FCSTD DOCUMENT  (FreeCAD 0.17R13541 (Git))
Label: Infineon_PG-LLGA-5-1
License: All rights reserved
LicenseURL: http://en.wikipedia.org/wiki/All_rights_reserved
objects: Sketcher::SketchObject×16, App::Annotation×2, App::DocumentObjectGroup×1
note: 16 computed .brp shape members not serialized (recipe doc carries the construction recipe); baked Part::Feature solids carry a one-line shape summary decoded from their .brp

FEATURE [Sketcher::SketchObject] Sketch  label="F_Fab_0.1"
  sketch-geometry (5):
    g0: LineSegment StartX=2 StartY=1.5 StartZ=0 EndX=2 EndY=-1.5 EndZ=0
    g1: LineSegment StartX=2 StartY=-1.5 StartZ=0 EndX=-2 EndY=-1.5 EndZ=0
    g2: LineSegment StartX=-2 StartY=-1.5 StartZ=0 EndX=-2 EndY=0.5 EndZ=0
    g3: LineSegment StartX=2 StartY=1.5 StartZ=0 EndX=-1 EndY=1.5 EndZ=0
    g4: LineSegment StartX=-2 StartY=0.5 StartZ=0 EndX=-1 EndY=1.5 EndZ=0
  constraints (14):
    c: Coincident(g0,g1)
    c: Coincident(g1,g2)
    c: Horizontal(g1)
    c: Vertical(g0)
    c: Vertical(g2)
    c: Symmetric(g1,g0,g-1)
    c: DistanceY(g0,g0) = 3
    c: DistanceX(g1,g0) = 4
    c: DistanceY(g2,g0) = 1
    c: Coincident(g3,g0)
    c: Horizontal(g3)
    c: DistanceX(g2,g3) = 1
    c: Coincident(g4,g2)
    c: Coincident(g4,g3)
FEATURE [Sketcher::SketchObject] Sketch001  label="F_CrtYd_0.05"
  MapMode = 2
  Support = -> [Sketch]
  sketch-geometry (4):
    g0: LineSegment StartX=-2.25 StartY=1.75 StartZ=0 EndX=2.25 EndY=1.75 EndZ=0
    g1: LineSegment StartX=2.25 StartY=1.75 StartZ=0 EndX=2.25 EndY=-1.75 EndZ=0
    g2: LineSegment StartX=2.25 StartY=-1.75 StartZ=0 EndX=-2.25 EndY=-1.75 EndZ=0
    g3: LineSegment StartX=-2.25 StartY=-1.75 StartZ=0 EndX=-2.25 EndY=1.75 EndZ=0
  constraints (11):
    c: Coincident(g0,g1)
    c: Coincident(g1,g2)
    c: Coincident(g2,g3)
    c: Coincident(g3,g0)
    c: Horizontal(g0)
    c: Horizontal(g2)
    c: Vertical(g1)
    c: Vertical(g3)
    c: DistanceX(g2,g2) = 4.5
    c: DistanceY(g1,g1) = 3.5
    c: Symmetric(g1,g0,g-1)
FEATURE [Sketcher::SketchObject] Sketch002  label="F_Silks_0.12"
  MapMode = 2
  Support = -> [Sketch001]
  sketch-geometry (4):
    g0: LineSegment StartX=-2.11 StartY=1.61 StartZ=0 EndX=2.11 EndY=1.61 EndZ=0
    g1: LineSegment StartX=2.11 StartY=1.61 StartZ=0 EndX=2.11 EndY=-1.61 EndZ=0
    g2: LineSegment StartX=2.11 StartY=-1.61 StartZ=0 EndX=-2.11 EndY=-1.61 EndZ=0
    g3: LineSegment StartX=-2.11 StartY=-1.61 StartZ=0 EndX=-2.11 EndY=1.61 EndZ=0
  constraints (11):
    c: Coincident(g0,g1)
    c: Coincident(g1,g2)
    c: Coincident(g2,g3)
    c: Coincident(g3,g0)
    c: Horizontal(g0)
    c: Horizontal(g2)
    c: Vertical(g1)
    c: Vertical(g3)
    c: DistanceX(g2,g2) = 4.22
    c: DistanceY(g1,g1) = 3.22
    c: Symmetric(g1,g0,g-1)
FEATURE [Sketcher::SketchObject] Sketch003  label="Pads_NPTH"
  sketch-geometry (1):
    g0: Circle CenterX=0.68 CenterY=0 CenterZ=0 NormalX=0 NormalY=0 NormalZ=1 AngleXU=0 Radius=0.4
  constraints (3):
    c: PointOnObject(g0,g-1)
    c: Radius(g0) = 0.4
    c: DistanceX(g-1,g0) = 0.68
FEATURE [Sketcher::SketchObject] Sketch005  label="Pads_TH_SMD"
  MapMode = 2
  sketch-geometry (19):
    g0: LineSegment StartX=-1.275 StartY=1.2 StartZ=0 EndX=-1.725 EndY=1.2 EndZ=0
    g1: LineSegment StartX=-1.725 StartY=1.2 StartZ=0 EndX=-1.725 EndY=0.5 EndZ=0
    g2: LineSegment StartX=-1.725 StartY=0.5 StartZ=0 EndX=-1.275 EndY=0.5 EndZ=0
    g3: LineSegment StartX=-1.275 StartY=0.5 StartZ=0 EndX=-1.275 EndY=1.2 EndZ=0
    g4: GeomPoint X=-1.5 Y=0.5 Z=0
    g5: GeomPoint X=-1.725 Y=0.85 Z=0
    g6: LineSegment StartX=-1.025 StartY=1.2 StartZ=0 EndX=-0.575 EndY=1.2 EndZ=0
    g7: LineSegment StartX=-0.575 StartY=1.2 StartZ=0 EndX=-0.575 EndY=0.5 EndZ=0
    g8: LineSegment StartX=-0.575 StartY=0.5 StartZ=0 EndX=-1.025 EndY=0.5 EndZ=0
    g9: LineSegment StartX=-1.025 StartY=0.5 StartZ=0 EndX=-1.025 EndY=1.2 EndZ=0
    g10: LineSegment StartX=-1.725 StartY=-0.5 StartZ=0 EndX=-1.275 EndY=-0.5 EndZ=0
    g11: LineSegment StartX=-1.275 StartY=-0.5 StartZ=0 EndX=-1.275 EndY=-1.2 EndZ=0
    g12: LineSegment StartX=-1.275 StartY=-1.2 StartZ=0 EndX=-1.725 EndY=-1.2 EndZ=0
    g13: LineSegment StartX=-1.725 StartY=-1.2 StartZ=0 EndX=-1.725 EndY=-0.5 EndZ=0
    g14: LineSegment StartX=-1.025 StartY=-0.5 StartZ=0 EndX=-0.575 EndY=-0.5 EndZ=0
    g15: LineSegment StartX=-0.575 StartY=-0.5 StartZ=0 EndX=-0.575 EndY=-1.2 EndZ=0
    g16: LineSegment StartX=-0.575 StartY=-1.2 StartZ=0 EndX=-1.025 EndY=-1.2 EndZ=0
    g17: LineSegment StartX=-1.025 StartY=-1.2 StartZ=0 EndX=-1.025 EndY=-0.5 EndZ=0
    g18: GeomPoint X=-1.725 Y=-0.85 Z=0
  constraints (54):
    c: Coincident(g0,g1)
    c: Coincident(g1,g2)
    c: Coincident(g2,g3)
    c: Coincident(g3,g0)
    c: Horizontal(g0)
    c: Horizontal(g2)
    c: Vertical(g1)
    c: Vertical(g3)
    c: DistanceX(g2,g2) = 0.45
    c: DistanceY(g3,g3) = 0.7
    c: PointOnObject(g4,g2)
    c: Symmetric(g2,g1,g4)
    c: PointOnObject(g5,g1)
    c: Symmetric(g0,g1,g5)
    c: DistanceY(g-1,g5) = 0.85
    c: DistanceX(g4,g-1) = 1.5
    c: Coincident(g6,g7)
    c: Coincident(g7,g8)
    c: Coincident(g8,g9)
    c: Coincident(g9,g6)
    c: Horizontal(g6)
    c: Horizontal(g8)
    c: Vertical(g7)
    c: Vertical(g9)
    c: Coincident(g10,g11)
    c: Coincident(g11,g12)
    c: Coincident(g12,g13)
    c: Coincident(g13,g10)
    c: Horizontal(g10)
    c: Horizontal(g12)
    c: Vertical(g11)
    c: Vertical(g13)
    c: Coincident(g14,g15)
    c: Coincident(g15,g16)
    c: Coincident(g16,g17)
    c: Coincident(g17,g14)
    c: Horizontal(g14)
    c: Horizontal(g16)
    c: Vertical(g15)
    c: Vertical(g17)
    c: Equal(g3,g7)
    c: Equal(g7,g15)
    c: Equal(g15,g11)
    c: Equal(g2,g8)
    c: Equal(g8,g14)
    c: Equal(g14,g10)
    c: PointOnObject(g18,g13)
    c: Symmetric(g12,g10,g18)
    c: DistanceY(g18,g5) = 1.7
    c: DistanceY(g0,g6) = 0
    c: DistanceX(g10,g2) = 0
    c: DistanceX(g14,g8) = 0
    c: DistanceY(g10,g14) = 0
    c: DistanceX(g2,g7) = 0.7
FEATURE [Sketcher::SketchObject] Sketch006  label="Pads_Poly_paste"
  MapMode = 2
  Support = -> [Sketch005]
  sketch-geometry (8):
    g0: ArcOfCircle CenterX=-1.5 CenterY=0.975 CenterZ=0 NormalX=0 NormalY=0 NormalZ=1 AngleXU=0 Radius=0.2 StartAngle=0 EndAngle=3.14159
    g1: ArcOfCircle CenterX=-1.5 CenterY=0.725 CenterZ=0 NormalX=0 NormalY=0 NormalZ=1 AngleXU=0 Radius=0.2 StartAngle=3.14159 EndAngle=6.28319
    g2: LineSegment StartX=-1.7 StartY=0.975 StartZ=0 EndX=-1.7 EndY=0.725 EndZ=0
    g3: LineSegment StartX=-1.3 StartY=0.975 StartZ=0 EndX=-1.3 EndY=0.725 EndZ=0
    g4: GeomPoint X=-1.5 Y=1.175 Z=0
    g5: GeomPoint X=-1.5 Y=0.525 Z=0
    g6: GeomPoint X=-1.5 Y=0.85 Z=0
    g7: Circle CenterX=-1.5 CenterY=0.725 CenterZ=0 NormalX=0 NormalY=0 NormalZ=1 AngleXU=0 Radius=0.15
  constraints (17):
    c: Tangent(g0,g3) = 1.5708
    c: Tangent(g0,g2) = -1.5708
    c: Tangent(g2,g1) = -1.5708
    c: Tangent(g3,g1) = 1.5708
    c: Vertical(g2)
    c: Equal(g0,g1)
    c: DistanceX(g0,g0) = 0.4
    c: PointOnObject(g4,g0)
    c: PointOnObject(g5,g1)
    c: Vertical(g5,g1)
    c: Vertical(g0,g4)
    c: DistanceY(g5,g4) = 0.65
    c: DistanceX(g5,g-1) = 1.5
    c: Symmetric(g0,g1,g6)
    c: DistanceY(g-1,g6) = 0.85
    c: Coincident(g7,g1)
    c: Radius(g7) = 0.15
FEATURE [App::Annotation] Text  label="Ref#_1mm"
  LabelText = REF**
  Position = (0,2.5,0)
FEATURE [App::Annotation] Text001  label="Value#_1.00mm"
  LabelText = Infineon_PG-LLGA-5-1
  Position = (0,-2.5,0)
FEATURE [Sketcher::SketchObject] Sketch008  label="Pads_Geom_0.46"
  MapMode = 2
  sketch-geometry (2):
    g0: Circle CenterX=0.68 CenterY=0 CenterZ=0 NormalX=0 NormalY=0 NormalZ=1 AngleXU=0 Radius=0.81
    g1: Circle [constr] CenterX=0.68 CenterY=0.81 CenterZ=0 NormalX=0 NormalY=0 NormalZ=1 AngleXU=0 Radius=0.2
  constraints (6):
    c: Radius(g0) = 0.81
    c: DistanceX(g-1,g0) = 0.68
    c: PointOnObject(g0,g-1)
    c: PointOnObject(g1,g0)
    c: Radius(g1) = 0.2
    c: Vertical(g1,g0)
FEATURE [Sketcher::SketchObject] Sketch009  label="Pads_Poly_paste001"
  MapMode = 2
  Support = -> [Sketch005]
  sketch-geometry (8):
    g0: ArcOfCircle CenterX=-0.8 CenterY=0.975 CenterZ=0 NormalX=0 NormalY=0 NormalZ=1 AngleXU=0 Radius=0.2 StartAngle=0 EndAngle=3.14159
    g1: LineSegment StartX=-1 StartY=0.975 StartZ=0 EndX=-1 EndY=0.725 EndZ=0
    g2: LineSegment StartX=-0.6 StartY=0.975 StartZ=0 EndX=-0.6 EndY=0.725 EndZ=0
    g3: GeomPoint X=-0.8 Y=1.175 Z=0
    g4: GeomPoint X=-0.8 Y=0.525 Z=0
    g5: GeomPoint X=-0.8 Y=0.85 Z=0
    g6: ArcOfCircle CenterX=-0.8 CenterY=0.725 CenterZ=0 NormalX=0 NormalY=0 NormalZ=1 AngleXU=0 Radius=0.2 StartAngle=3.14159 EndAngle=6.28319
    g7: Circle CenterX=-0.8 CenterY=0.725 CenterZ=0 NormalX=0 NormalY=0 NormalZ=1 AngleXU=0 Radius=0.15
  constraints (19):
    c: Tangent(g0,g2) = 1.5708
    c: Tangent(g0,g1) = -1.5708
    c: Vertical(g1)
    c: PointOnObject(g3,g0)
    c: DistanceY(g4,g3) = 0.65
    c: DistanceX(g0,g0) = 0.4
    c: Coincident(g6,g1)
    c: Coincident(g6,g2)
    c: PointOnObject(g4,g6)
    c: Symmetric(g0,g6,g5)
    c: DistanceY(g-1,g5) = 0.85
    c: DistanceX(g4,g-1) = 0.8
    c: Tangent(g2,g6) = 1.5708
    c: Tangent(g1,g6) = -1.5708
    c: Vertical(g2)
    c: Vertical(g3,g0)
    c: Vertical(g6,g4)
    c: Coincident(g7,g6)
    c: Radius(g7) = 0.15
FEATURE [Sketcher::SketchObject] Sketch010  label="Pads_Poly_paste002"
  MapMode = 2
  Support = -> [Sketch005]
  sketch-geometry (8):
    g0: ArcOfCircle CenterX=-1.5 CenterY=-0.725 CenterZ=0 NormalX=0 NormalY=0 NormalZ=1 AngleXU=0 Radius=0.2 StartAngle=0 EndAngle=3.14159
    g1: ArcOfCircle CenterX=-1.5 CenterY=-0.975 CenterZ=0 NormalX=0 NormalY=0 NormalZ=1 AngleXU=0 Radius=0.2 StartAngle=3.14159 EndAngle=6.28319
    g2: LineSegment StartX=-1.7 StartY=-0.725 StartZ=0 EndX=-1.7 EndY=-0.975 EndZ=0
    g3: LineSegment StartX=-1.3 StartY=-0.725 StartZ=0 EndX=-1.3 EndY=-0.975 EndZ=0
    g4: GeomPoint X=-1.5 Y=-0.85 Z=0
    g5: Circle CenterX=-1.5 CenterY=-0.725 CenterZ=0 NormalX=0 NormalY=0 NormalZ=1 AngleXU=0 Radius=0.15
    g6: GeomPoint X=-1.5 Y=-0.525 Z=0
    g7: GeomPoint X=-1.5 Y=-1.175 Z=0
  constraints (17):
    c: Tangent(g0,g3) = 1.5708
    c: Tangent(g0,g2) = -1.5708
    c: Tangent(g2,g1) = -1.5708
    c: Tangent(g3,g1) = 1.5708
    c: Vertical(g2)
    c: Equal(g0,g1)
    c: Symmetric(g0,g1,g4)
    c: Coincident(g5,g0)
    c: PointOnObject(g6,g0)
    c: PointOnObject(g7,g1)
    c: Vertical(g1,g7)
    c: Vertical(g6,g0)
    c: DistanceX(g6,g-1) = 1.5
    c: DistanceY(g4,g-1) = 0.85
    c: DistanceX(g1,g1) = 0.4
    c: DistanceY(g7,g6) = 0.65
    c: Radius(g5) = 0.15
FEATURE [Sketcher::SketchObject] Sketch011  label="Pads_Poly_paste003"
  MapMode = 2
  Support = -> [Sketch005]
  sketch-geometry (8):
    g0: ArcOfCircle CenterX=-0.8 CenterY=-0.725 CenterZ=0 NormalX=0 NormalY=0 NormalZ=1 AngleXU=0 Radius=0.2 StartAngle=0 EndAngle=3.14159
    g1: ArcOfCircle CenterX=-0.8 CenterY=-0.975 CenterZ=0 NormalX=0 NormalY=0 NormalZ=1 AngleXU=0 Radius=0.2 StartAngle=3.14159 EndAngle=6.28319
    g2: LineSegment StartX=-1 StartY=-0.725 StartZ=0 EndX=-1 EndY=-0.975 EndZ=0
    g3: LineSegment StartX=-0.6 StartY=-0.725 StartZ=0 EndX=-0.6 EndY=-0.975 EndZ=0
    g4: Circle CenterX=-0.8 CenterY=-0.725 CenterZ=0 NormalX=0 NormalY=0 NormalZ=1 AngleXU=0 Radius=0.15
    g5: GeomPoint X=-0.8 Y=-0.525 Z=0
    g6: GeomPoint X=-0.8 Y=-0.85 Z=0
    g7: GeomPoint X=-0.8 Y=-1.175 Z=0
  constraints (17):
    c: Tangent(g0,g3) = 1.5708
    c: Tangent(g0,g2) = -1.5708
    c: Tangent(g2,g1) = -1.5708
    c: Tangent(g3,g1) = 1.5708
    c: Vertical(g2)
    c: Equal(g0,g1)
    c: Coincident(g4,g0)
    c: PointOnObject(g5,g0)
    c: PointOnObject(g7,g1)
    c: Vertical(g5,g0)
    c: Symmetric(g0,g1,g6)
    c: Vertical(g1,g7)
    c: DistanceX(g6,g-1) = 0.8
    c: DistanceY(g6,g-1) = 0.85
    c: Radius(g4) = 0.15
    c: DistanceY(g7,g5) = 0.65
    c: DistanceX(g1,g1) = 0.4
FEATURE [Sketcher::SketchObject] Sketch012  label="Pads_Poly_paste004"
  MapMode = 2
  Support = -> [Sketch005]
  sketch-geometry (8):
    g0: GeomPoint X=0.68 Y=0 Z=0
    g1: LineSegment [constr] StartX=0.68 StartY=0 StartZ=0 EndX=1.75638 EndY=0.530474 EndZ=0
    g2: LineSegment [constr] StartX=0.68 StartY=0 StartZ=0 EndX=1.75638 EndY=-0.530474 EndZ=0
    g3: Circle CenterX=1.48 CenterY=0 CenterZ=0 NormalX=0 NormalY=0 NormalZ=1 AngleXU=0 Radius=0.15
    g4: ArcOfCircle CenterX=0.68 CenterY=0 CenterZ=0 NormalX=0 NormalY=0 NormalZ=1 AngleXU=0 Radius=0.6 StartAngle=6.07797 EndAngle=6.4884
    g5: ArcOfCircle CenterX=0.68 CenterY=0 CenterZ=0 NormalX=0 NormalY=0 NormalZ=1 AngleXU=0 Radius=1 StartAngle=6.07797 EndAngle=6.4884
    g6: ArcOfCircle CenterX=1.46321 CenterY=0.163023 CenterZ=0 NormalX=0 NormalY=0 NormalZ=1 AngleXU=0 Radius=0.2 StartAngle=0.205216 EndAngle=3.34681
    g7: ArcOfCircle CenterX=1.46321 CenterY=-0.163023 CenterZ=0 NormalX=0 NormalY=0 NormalZ=1 AngleXU=0 Radius=0.2 StartAngle=2.93638 EndAngle=6.07797
  constraints (23):
    c: PointOnObject(g0,g-1)
    c: DistanceX(g-1,g0) = 0.68
    c: Coincident(g1,g0)
    c: Coincident(g2,g0)
    c: Angle(g2,g1) = 0.915792
    c: Distance(g1) = 1.2
    c: Equal(g1,g2)
    c: Symmetric(g1,g2,g-1)
    c: PointOnObject(g3,g-1)
    c: Radius(g3) = 0.15
    c: DistanceX(g0,g3) = 0.8
    c: Coincident(g4,g0)
    c: Coincident(g5,g0)
    c: Radius(g5) = 1
    c: Radius(g4) = 0.6
    c: Tangent(g6,g1)
    c: Radius(g6) = 0.2
    c: Equal(g6,g7)
    c: Tangent(g7,g2)
    c: Tangent(g6,g4) = 1.5708
    c: Tangent(g6,g5) = -1.5708
    c: Tangent(g7,g5) = -1.5708
    c: Tangent(g7,g4) = 1.5708
FEATURE [Sketcher::SketchObject] Sketch013  label="Pads_Poly_paste005"
  MapMode = 2
  Support = -> [Sketch005]
  sketch-geometry (10):
    g0: GeomPoint X=0.68 Y=0 Z=0
    g1: LineSegment [constr] StartX=0.68 StartY=0 StartZ=0 EndX=1.6776 EndY=-0.666928 EndZ=0
    g2: LineSegment [constr] StartX=0.68 StartY=0 StartZ=0 EndX=0.758797 EndY=-1.19741 EndZ=0
    g3: ArcOfCircle CenterX=0.68 CenterY=0 CenterZ=0 NormalX=0 NormalY=0 NormalZ=1 AngleXU=0 Radius=0.6 StartAngle=5.03078 EndAngle=5.44121
    g4: ArcOfCircle CenterX=0.68 CenterY=0 CenterZ=0 NormalX=0 NormalY=0 NormalZ=1 AngleXU=0 Radius=1 StartAngle=5.03078 EndAngle=5.44121
    g5: ArcOfCircle CenterX=1.21279 CenterY=-0.596767 CenterZ=0 NormalX=0 NormalY=0 NormalZ=1 AngleXU=0 Radius=0.2 StartAngle=5.44121 EndAngle=8.5828
    g6: ArcOfCircle CenterX=0.930432 CenterY=-0.759792 CenterZ=0 NormalX=0 NormalY=0 NormalZ=1 AngleXU=0 Radius=0.2 StartAngle=1.88919 EndAngle=5.03078
    g7: Circle [constr] CenterX=0.68 CenterY=0 CenterZ=0 NormalX=0 NormalY=0 NormalZ=1 AngleXU=0 Radius=0.8
    g8: Circle CenterX=1.08001 CenterY=-0.692817 CenterZ=0 NormalX=0 NormalY=0 NormalZ=1 AngleXU=0 Radius=0.15
    g9: LineSegment [constr] StartX=0.68 StartY=0 StartZ=0 EndX=1.28001 EndY=-1.03923 EndZ=0
  constraints (28):
    c: PointOnObject(g0,g-1)
    c: DistanceX(g-1,g0) = 0.68
    c: Coincident(g1,g0)
    c: Distance(g1) = 1.2
    c: Angle(g-1,g1) = 2.5523
    c: Coincident(g2,g0)
    c: Equal(g1,g2)
    c: Angle(g2,g1) = 0.915792
    c: Coincident(g3,g0)
    c: Coincident(g4,g0)
    c: Tangent(g5,g1)
    c: Radius(g3) = 0.6
    c: Radius(g4) = 1
    c: Radius(g5) = 0.2
    c: Equal(g5,g6)
    c: Tangent(g6,g2)
    c: Tangent(g5,g3) = 1.5708
    c: Tangent(g5,g4) = -1.5708
    c: Tangent(g6,g4) = -1.5708
    c: Tangent(g6,g3) = 1.5708
    c: Radius(g7) = 0.8
    c: Coincident(g7,g0)
    c: PointOnObject(g8,g7)
    c: Radius(g8) = 0.15
    c: Coincident(g9,g0)
    c: Equal(g1,g9)
    c: Angle(g9,g1) = 0.457896
    c: PointOnObject(g8,g9)
FEATURE [Sketcher::SketchObject] Sketch014  label="Pads_Poly_paste006"
  MapMode = 2
  Support = -> [Sketch005]
  sketch-geometry (10):
    g0: GeomPoint X=0.68 Y=0 Z=0
    g1: LineSegment [constr] StartX=0.68 StartY=0 StartZ=0 EndX=0.601307 EndY=-1.19742 EndZ=0
    g2: LineSegment [constr] StartX=0.68 StartY=0 StartZ=0 EndX=-0.317542 EndY=-0.667015 EndZ=0
    g3: ArcOfCircle CenterX=0.68 CenterY=0 CenterZ=0 NormalX=0 NormalY=0 NormalZ=1 AngleXU=0 Radius=0.6 StartAngle=3.98365 EndAngle=4.39408
    g4: ArcOfCircle CenterX=0.68 CenterY=0 CenterZ=0 NormalX=0 NormalY=0 NormalZ=1 AngleXU=0 Radius=1 StartAngle=3.98365 EndAngle=4.39408
    g5: ArcOfCircle CenterX=0.429635 CenterY=-0.759814 CenterZ=0 NormalX=0 NormalY=0 NormalZ=1 AngleXU=0 Radius=0.2 StartAngle=4.39408 EndAngle=7.53568
    g6: ArcOfCircle CenterX=0.147258 CenterY=-0.596813 CenterZ=0 NormalX=0 NormalY=0 NormalZ=1 AngleXU=0 Radius=0.2 StartAngle=0.84206 EndAngle=3.98365
    g7: Circle [constr] CenterX=0.68 CenterY=0 CenterZ=0 NormalX=0 NormalY=0 NormalZ=1 AngleXU=0 Radius=0.8
    g8: Circle CenterX=0.280054 CenterY=-0.692852 CenterZ=0 NormalX=0 NormalY=0 NormalZ=1 AngleXU=0 Radius=0.15
    g9: LineSegment [constr] StartX=0.68 StartY=0 StartZ=0 EndX=0.0800816 EndY=-1.03928 EndZ=0
  constraints (28):
    c: PointOnObject(g0,g-1)
    c: DistanceX(g-1,g0) = 0.68
    c: Coincident(g1,g0)
    c: Distance(g1) = 1.2
    c: Angle(g-1,g1) = 1.50517
    c: Coincident(g2,g0)
    c: Equal(g1,g2)
    c: Angle(g2,g1) = 0.915792
    c: Coincident(g3,g0)
    c: Coincident(g4,g0)
    c: Tangent(g5,g1)
    c: Radius(g3) = 0.6
    c: Radius(g4) = 1
    c: Radius(g5) = 0.2
    c: Equal(g5,g6)
    c: Tangent(g6,g2)
    c: Tangent(g5,g3) = 1.5708
    c: Tangent(g5,g4) = -1.5708
    c: Tangent(g6,g4) = -1.5708
    c: Tangent(g6,g3) = 1.5708
    c: Radius(g7) = 0.8
    c: Coincident(g7,g0)
    c: PointOnObject(g8,g7)
    c: Radius(g8) = 0.15
    c: Coincident(g9,g0)
    c: Equal(g1,g9)
    c: Angle(g9,g1) = 0.457896
    c: PointOnObject(g8,g9)
FEATURE [Sketcher::SketchObject] Sketch015  label="Pads_Poly_paste007"
  MapMode = 2
  Support = -> [Sketch005]
  sketch-geometry (10):
    g0: GeomPoint X=0.68 Y=0 Z=0
    g1: LineSegment [constr] StartX=0.68 StartY=0 StartZ=0 EndX=-0.396382 EndY=-0.530474 EndZ=0
    g2: LineSegment [constr] StartX=0.68 StartY=0 StartZ=0 EndX=-0.396382 EndY=0.530474 EndZ=0
    g3: ArcOfCircle CenterX=0.68 CenterY=0 CenterZ=0 NormalX=0 NormalY=0 NormalZ=1 AngleXU=0 Radius=0.6 StartAngle=2.93638 EndAngle=3.34681
    g4: ArcOfCircle CenterX=0.68 CenterY=0 CenterZ=0 NormalX=0 NormalY=0 NormalZ=1 AngleXU=0 Radius=1 StartAngle=2.93638 EndAngle=3.34681
    g5: ArcOfCircle CenterX=-0.103214 CenterY=-0.163023 CenterZ=0 NormalX=0 NormalY=0 NormalZ=1 AngleXU=0 Radius=0.2 StartAngle=3.34681 EndAngle=6.4884
    g6: ArcOfCircle CenterX=-0.103214 CenterY=0.163023 CenterZ=0 NormalX=0 NormalY=0 NormalZ=1 AngleXU=0 Radius=0.2 StartAngle=6.07797 EndAngle=9.21956
    g7: Circle [constr] CenterX=0.68 CenterY=0 CenterZ=0 NormalX=0 NormalY=0 NormalZ=1 AngleXU=0 Radius=0.8
    g8: Circle CenterX=-0.12 CenterY=0 CenterZ=0 NormalX=0 NormalY=0 NormalZ=1 AngleXU=0 Radius=0.15
    g9: LineSegment [constr] StartX=0.68 StartY=0 StartZ=0 EndX=-0.52 EndY=0 EndZ=0
  constraints (28):
    c: PointOnObject(g0,g-1)
    c: DistanceX(g-1,g0) = 0.68
    c: Coincident(g1,g0)
    c: Distance(g1) = 1.2
    c: Angle(g-1,g1) = 0.457896
    c: Coincident(g2,g0)
    c: Equal(g1,g2)
    c: Angle(g2,g1) = 0.915792
    c: Coincident(g3,g0)
    c: Coincident(g4,g0)
    c: Tangent(g5,g1)
    c: Radius(g3) = 0.6
    c: Radius(g4) = 1
    c: Radius(g5) = 0.2
    c: Equal(g5,g6)
    c: Tangent(g6,g2)
    c: Tangent(g5,g3) = 1.5708
    c: Tangent(g5,g4) = -1.5708
    c: Tangent(g6,g4) = -1.5708
    c: Tangent(g6,g3) = 1.5708
    c: Radius(g7) = 0.8
    c: Coincident(g7,g0)
    c: PointOnObject(g8,g7)
    c: Radius(g8) = 0.15
    c: Coincident(g9,g0)
    c: Equal(g1,g9)
    c: Angle(g9,g1) = 0.457896
    c: PointOnObject(g8,g9)
FEATURE [Sketcher::SketchObject] Sketch016  label="Pads_Poly_paste008"
  MapMode = 2
  Support = -> [Sketch005]
  sketch-geometry (10):
    g0: GeomPoint X=0.68 Y=0 Z=0
    g1: LineSegment [constr] StartX=0.68 StartY=0 StartZ=0 EndX=-0.317595 EndY=0.666937 EndZ=0
    g2: LineSegment [constr] StartX=0.68 StartY=0 StartZ=0 EndX=0.601213 EndY=1.19741 EndZ=0
    g3: ArcOfCircle CenterX=0.68 CenterY=0 CenterZ=0 NormalX=0 NormalY=0 NormalZ=1 AngleXU=0 Radius=0.6 StartAngle=1.88918 EndAngle=2.29961
    g4: ArcOfCircle CenterX=0.68 CenterY=0 CenterZ=0 NormalX=0 NormalY=0 NormalZ=1 AngleXU=0 Radius=1 StartAngle=1.88918 EndAngle=2.29961
    g5: ArcOfCircle CenterX=0.147211 CenterY=0.596772 CenterZ=0 NormalX=0 NormalY=0 NormalZ=1 AngleXU=0 Radius=0.2 StartAngle=2.29961 EndAngle=5.4412
    g6: ArcOfCircle CenterX=0.429575 CenterY=0.759794 CenterZ=0 NormalX=0 NormalY=0 NormalZ=1 AngleXU=0 Radius=0.2 StartAngle=5.03077 EndAngle=8.17236
    g7: Circle [constr] CenterX=0.68 CenterY=0 CenterZ=0 NormalX=0 NormalY=0 NormalZ=1 AngleXU=0 Radius=0.8
    g8: Circle CenterX=0.28 CenterY=0.69282 CenterZ=0 NormalX=0 NormalY=0 NormalZ=1 AngleXU=0 Radius=0.15
    g9: LineSegment [constr] StartX=0.68 StartY=0 StartZ=0 EndX=0.08 EndY=1.03923 EndZ=0
  constraints (28):
    c: PointOnObject(g0,g-1)
    c: DistanceX(g-1,g0) = 0.68
    c: Coincident(g1,g0)
    c: Distance(g1) = 1.2
    c: Coincident(g2,g0)
    c: Equal(g1,g2)
    c: Angle(g2,g1) = 0.915792
    c: Coincident(g3,g0)
    c: Coincident(g4,g0)
    c: Tangent(g5,g1)
    c: Radius(g3) = 0.6
    c: Radius(g4) = 1
    c: Radius(g5) = 0.2
    c: Equal(g5,g6)
    c: Tangent(g6,g2)
    c: Tangent(g5,g3) = 1.5708
    c: Tangent(g5,g4) = -1.5708
    c: Tangent(g6,g4) = -1.5708
    c: Tangent(g6,g3) = 1.5708
    c: Radius(g7) = 0.8
    c: Coincident(g7,g0)
    c: PointOnObject(g8,g7)
    c: Radius(g8) = 0.15
    c: Coincident(g9,g0)
    c: Equal(g1,g9)
    c: Angle(g9,g1) = 0.457896
    c: PointOnObject(g8,g9)
    c: Angle(g1,g-1) = 0.589302
FEATURE [Sketcher::SketchObject] Sketch017  label="Pads_Poly_paste009"
  MapMode = 2
  Support = -> [Sketch005]
  sketch-geometry (10):
    g0: GeomPoint X=0.68 Y=0 Z=0
    g1: LineSegment [constr] StartX=0.68 StartY=0 StartZ=0 EndX=0.758787 EndY=1.19741 EndZ=0
    g2: LineSegment [constr] StartX=0.68 StartY=0 StartZ=0 EndX=1.67759 EndY=0.666937 EndZ=0
    g3: ArcOfCircle CenterX=0.68 CenterY=0 CenterZ=0 NormalX=0 NormalY=0 NormalZ=1 AngleXU=0 Radius=0.6 StartAngle=0.841982 EndAngle=1.25241
    g4: ArcOfCircle CenterX=0.68 CenterY=0 CenterZ=0 NormalX=0 NormalY=0 NormalZ=1 AngleXU=0 Radius=1 StartAngle=0.841982 EndAngle=1.25241
    g5: ArcOfCircle CenterX=0.930425 CenterY=0.759794 CenterZ=0 NormalX=0 NormalY=0 NormalZ=1 AngleXU=0 Radius=0.2 StartAngle=1.25241 EndAngle=4.39401
    g6: ArcOfCircle CenterX=1.21279 CenterY=0.596772 CenterZ=0 NormalX=0 NormalY=0 NormalZ=1 AngleXU=0 Radius=0.2 StartAngle=3.98357 EndAngle=7.12517
    g7: Circle [constr] CenterX=0.68 CenterY=0 CenterZ=0 NormalX=0 NormalY=0 NormalZ=1 AngleXU=0 Radius=0.8
    g8: Circle CenterX=1.08 CenterY=0.69282 CenterZ=0 NormalX=0 NormalY=0 NormalZ=1 AngleXU=0 Radius=0.15
    g9: LineSegment [constr] StartX=0.68 StartY=0 StartZ=0 EndX=1.28 EndY=1.03923 EndZ=0
  constraints (28):
    c: PointOnObject(g0,g-1)
    c: DistanceX(g-1,g0) = 0.68
    c: Coincident(g1,g0)
    c: Distance(g1) = 1.2
    c: Coincident(g2,g0)
    c: Equal(g1,g2)
    c: Angle(g2,g1) = 0.915792
    c: Coincident(g3,g0)
    c: Coincident(g4,g0)
    c: Tangent(g5,g1)
    c: Radius(g3) = 0.6
    c: Radius(g4) = 1
    c: Radius(g5) = 0.2
    c: Equal(g5,g6)
    c: Tangent(g6,g2)
    c: Tangent(g5,g3) = 1.5708
    c: Tangent(g5,g4) = -1.5708
    c: Tangent(g6,g4) = -1.5708
    c: Tangent(g6,g3) = 1.5708
    c: Radius(g7) = 0.8
    c: Coincident(g7,g0)
    c: PointOnObject(g8,g7)
    c: Radius(g8) = 0.15
    c: Coincident(g9,g0)
    c: Equal(g1,g9)
    c: Angle(g9,g1) = 0.457896
    c: PointOnObject(g8,g9)
    c: Angle(g1,g-1) = 1.6365
FEATURE [App::DocumentObjectGroup] Group  label="Infineon_PG-LLGA-5-1"
  Group = -> [Sketch,Sketch001,Sketch002,Sketch003,Sketch005,Sketch006,Text,Text001,Sketch008,Sketch009,Sketch010,Sketch011,Sketch012,Sketch013,Sketch014,Sketch015,Sketch016,Sketch017]
